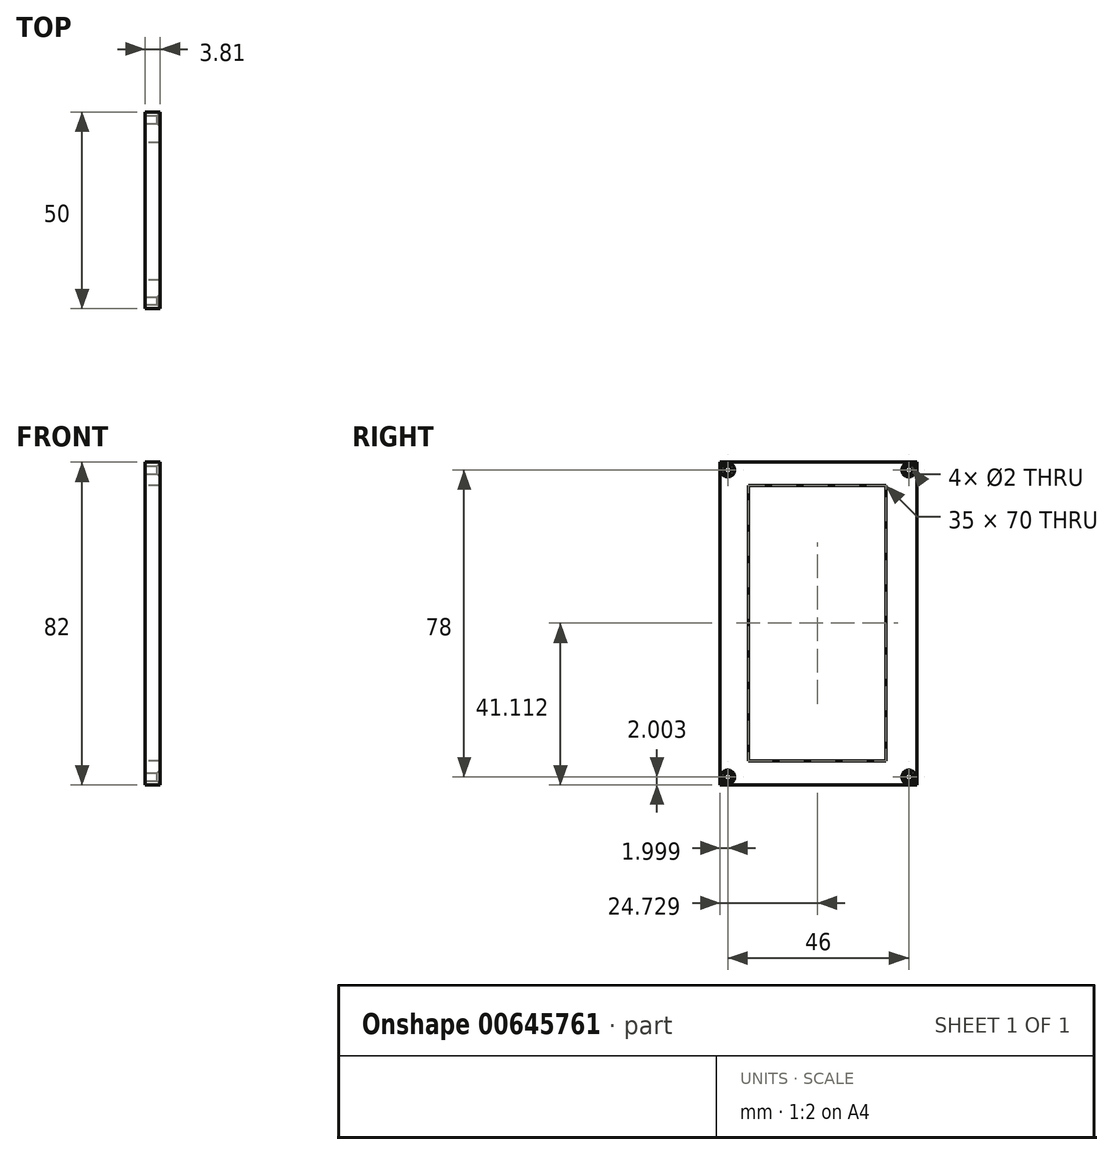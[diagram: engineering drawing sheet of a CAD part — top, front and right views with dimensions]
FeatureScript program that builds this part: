
annotation { "Feature Type Name" : "Feature", "Feature Type Description" : "" }
export const myFeature = defineFeature(function(context is Context, id is Id, definition is map)
    precondition{}
    {
        {
            var Q0;
            Q0=qCreatedBy(makeId("Right.planeOp"),FACE);
            var sketch = newSketch(context, id + "F0", { "sketchPlane" : qUnion([Q0])});
            skLineSegment(sketch, "E0.bottom", {"start": v(-26, 47.9) * mm, "end": v(24, 47.9) * mm});
            skLineSegment(sketch, "E0.top", {"start": v(-26, -34.1) * mm, "end": v(24, -34.1) * mm});
            skLineSegment(sketch, "E0.left", {"start": v(-26, 47.9) * mm, "end": v(-26, -34.1) * mm});
            skLineSegment(sketch, "E0.right", {"start": v(24, 47.9) * mm, "end": v(24, -34.1) * mm});
            skLineSegment(sketch, "E1", {"start": v(-18.76, 42.01) * mm, "end": v(16.24, 42.01) * mm});
            skLineSegment(sketch, "E2", {"start": v(16.24, 42.01) * mm, "end": v(16.24, -27.99) * mm});
            skLineSegment(sketch, "E3", {"start": v(16.24, -27.99) * mm, "end": v(-18.76, -27.99) * mm});
            skLineSegment(sketch, "E4", {"start": v(-18.76, -27.99) * mm, "end": v(-18.76, 42.01) * mm});
            skSolve(sketch);
        }
        {
            var Q0;
            Q0 = qSketchRegion(id + "F0", true);
            extrude(context, id + "F1", {"entities" : qUnion([Q0]), "depth" : 3.8 * mm, "offsetDistance" : 25.4 * mm});
        }
        {
            var Q0;
            Q0=makeQuery(id+"F1.opExtrude","CAP_FACE",FACE,{"disambiguationData":[OSD([sQuery(id+"F0.wireOp",EDGE,"E0.bottom"),sQuery(id+"F0.wireOp",EDGE,"E0.top"),sQuery(id+"F0.wireOp",EDGE,"E0.left"),sQuery(id+"F0.wireOp",EDGE,"E0.right")])],"isStart":false});
            var sketch = newSketch(context, id + "F2", { "sketchPlane" : qUnion([Q0])});
            skPoint(sketch, "E5", {"position": v(-24, 45.9) * mm});
            skPoint(sketch, "E6", {"position": v(22, 45.9) * mm});
            skPoint(sketch, "E7", {"position": v(22, -32.1) * mm});
            skPoint(sketch, "E8", {"position": v(-24, -32.1) * mm});
            skSolve(sketch);
        }
        {
            var Q0;
            Q0=sQuery(id+"F2.wireOp",VERTEX,"E5");
            var Q1;
            Q1=sQuery(id+"F2.wireOp",VERTEX,"E6");
            var Q2;
            Q2=sQuery(id+"F2.wireOp",VERTEX,"E7");
            var Q3;
            Q3=sQuery(id+"F2.wireOp",VERTEX,"E8");
            var Q4;
            Q4=makeQuery(id+"F1.opExtrude","SWEPT_BODY",BODY,{"disambiguationData":[OSD([sQuery(id+"F0.wireOp",EDGE,"E0.bottom"),sQuery(id+"F0.wireOp",EDGE,"E0.top"),sQuery(id+"F0.wireOp",EDGE,"E0.left"),sQuery(id+"F0.wireOp",EDGE,"E0.right")])]});
            hole(context, id + "F3", {"style" : HoleStyle.C_SINK, "endStyle" : HoleEndStyle.BLIND, "holeDiameter" : 2 * mm, "cSinkDiameter" : 3.5 * mm, "cSinkAngle" : 90 * degree, "majorDiameter" : 6.35 * mm, "holeDepth" : 50.8 * mm, "isTappedThrough" : true, "tappedDepth" : 12.7 * mm, "tapClearance" : 3, "locations" : qUnion([Q0, Q1, Q2, Q3]), "scope" : qUnion([Q4])});
        }
    });
